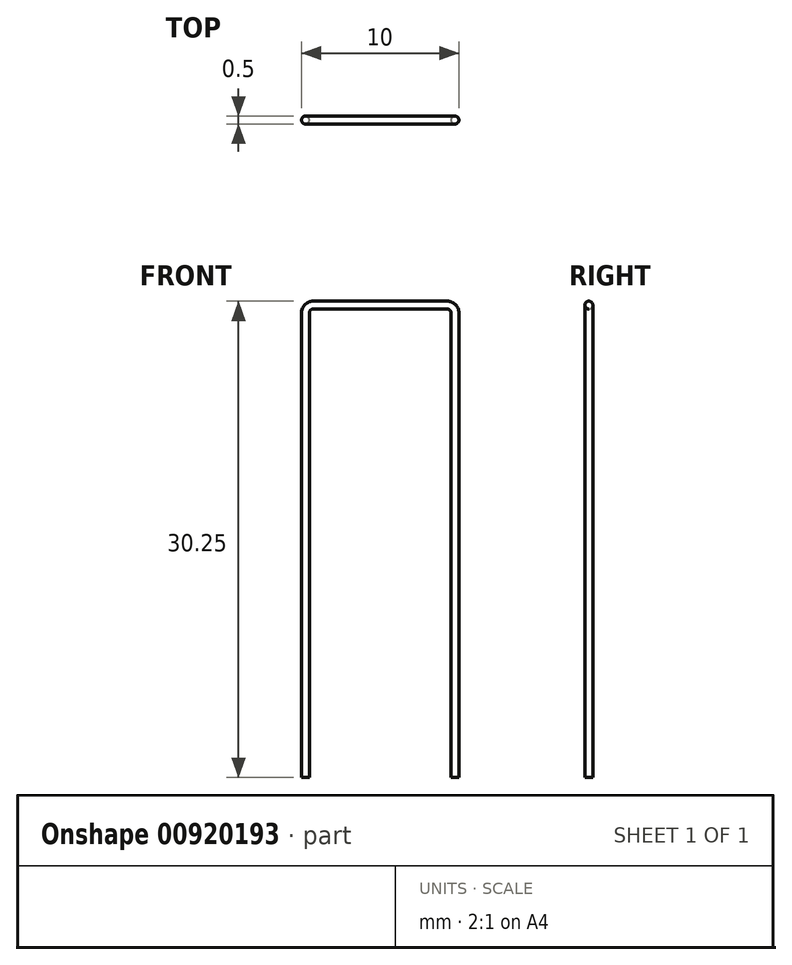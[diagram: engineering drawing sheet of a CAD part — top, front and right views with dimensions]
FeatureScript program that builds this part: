
annotation { "Feature Type Name" : "Feature", "Feature Type Description" : "" }
export const myFeature = defineFeature(function(context is Context, id is Id, definition is map)
    precondition{}
    {
        {
            var Q0;
            Q0=qCreatedBy(makeId("Top.planeOp"),FACE);
            var sketch = newSketch(context, id + "F0", { "sketchPlane" : qUnion([Q0])});
            skCircle(sketch, "E0", {"center": v(0, 0) * mm, "radius": 0.25 * mm});
            skSolve(sketch);
        }
        {
            var Q0;
            Q0=qCreatedBy(makeId("Front.planeOp"),FACE);
            var sketch = newSketch(context, id + "F1", { "sketchPlane" : qUnion([Q0])});
            skLineSegment(sketch, "E1", {"start": v(0, 0) * mm, "end": v(0, 29.5) * mm});
            skLineSegment(sketch, "E2", {"start": v(0.5, 30) * mm, "end": v(9, 30) * mm});
            skLineSegment(sketch, "E3", {"start": v(9.5, 29.5) * mm, "end": v(9.5, 0) * mm});
            skPoint(sketch, "E4.visualSharp", {"position": v(9.5, 30) * mm});
            skArc(sketch, "E4.filletArc", {"start": v(9.5, 29.5) * mm, "mid": v(9.35, 29.85) * mm, "end": v(9, 30) * mm});
            skPoint(sketch, "E5.visualSharp", {"position": v(0, 30) * mm});
            skArc(sketch, "E5.filletArc", {"start": v(0.5, 30) * mm, "mid": v(0.15, 29.85) * mm, "end": v(0, 29.5) * mm});
            skSolve(sketch);
        }
        {
            var Q0;
            Q0=makeQuery(id+"F0.imprint","IMPRINT",FACE,{"disambiguationData":[TD([[makeQuery(id+"F0.imprint","IMPRINT",EDGE,{"derivedFrom":sQuery(id+"F0.wireOp",EDGE,"E0")}),1.0]])]});
            var Q1;
            Q1=sQuery(id+"F1.wireOp",EDGE,"E1");
            var Q2;
            Q2=sQuery(id+"F1.wireOp",EDGE,"E5.filletArc");
            var Q3;
            Q3=sQuery(id+"F1.wireOp",EDGE,"E2");
            var Q4;
            Q4=sQuery(id+"F1.wireOp",EDGE,"E4.filletArc");
            var Q5;
            Q5=sQuery(id+"F1.wireOp",EDGE,"E3");
            sweep(context, id + "F2", {"profiles" : qUnion([Q0]), "path" : qUnion([Q1, Q2, Q3, Q4, Q5])});
        }
    });
